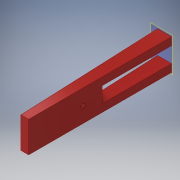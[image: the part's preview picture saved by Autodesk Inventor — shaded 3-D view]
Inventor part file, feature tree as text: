
AUTODESK INVENTOR PART (.ipt)
format: ipt  version: 2019.1 (Build 231200000, 200)  size: 157,184 bytes
history: native  units: in
note: dims shown in document units (in); Inventor stores cm internally (conversion verified against a paired STEP export)
features: sketch x5, extrude x4, plane x2, hole x1, split x1
ambient origin geometry x8: Origin, YZ Plane, XZ Plane, XY Plane, X Axis, Y Axis, Z Axis, Center Point
bodies: Solid1 (feature_tree)
feature tree (13):
  extrude  "Extrusion1"  Depth=0.0172in
  plane  "Work Plane1"
  extrude  "Extrusion2"  TaperAngle=0.0deg  [1 undecoded]
  hole  "Hole2"  [1 undecoded]
  extrude  "Extrusion3"  Depth=1.0in
  plane  "Work Plane2"
  split  "Split2"
  extrude  "Extrusion4"  Depth=0.4375in
  sketch  "Sketch1"  dims[d0=18.5in d1=0.0172in]
  sketch  "Sketch2"  dims[d2=2.0in d3=0.0in]
  sketch  "Sketch4"  dims[d4=0.5in d5=0.0in]
  sketch  "Sketch6"  dims[d16=1.0in d17=3.5in]
  sketch  "Sketch7"  dims[d18=13.625in d19=0.266in d20=0.75in d21=0.7in d22=1.65in d23=0.5635in d24=1.0in d25=0.8108in d26=0.4375in d27=0.92in d28=0.0in d29=-9.25in d30=1.0in d31=9.0in d32=1.0in d33=0.0in]
note: 2 required parameter values undecoded (feature->parameter linkage not recoverable at this tier; creation-order binding heuristic only, values carry confidence <= 0.55)
